# Revit family: Sanitary_Bath_Spas_Johnson-Suisse_Select_Mk_II_1600_Bath
name_source: partatom
category: Plumbing Fixtures
revit_build: Autodesk Revit 2015 (Build: 20140606_1530(x64)
units: mm (PartAtom-declared; Revit-internal decimal feet)

## types (1)
- Select Mk II 1600 Bath
    BIMobject category = Bath & Spas
    Brand url = http://www.johnsonsuisse.com.au
    Default Elevation = 1219 mm
    Design country = China
    EAN code = https://9325304005621
    Edition number = 1
    IFC Classification = Sanitary Terminal
    Manufacturer country = China
    Manufacturer name = Johnson Suisse
    Material main = Acrylic
    NBS Reference Code = 35-06-08
    NBS Reference Description = Baths
    Nominal height = 420 mm  [stored 1.37795 ft]
    Nominal width = 1660 mm  [stored 5.44619 ft]
    Product Guid = 1ae362b3-3b77-4cad-9836-f70f2127e520
    Product SKU = J5166
    Product data url = https://bimobject.com
    Product family = Select
    Product group = Baths
    Product url = https://johnsonsuisse.com.au
    QR code = http://bimobject.com
    Technical description = https://johnsonsuisse.com.au
    Type = select_mk_ii_1600_bath : Default
    UNSPSC Code = 30181501
    Uniclass 1.4 Code = L7211
    Uniclass 1.4 Description = Baths
    Uniclass 2.0 Code = PR-35-06-08
    Uniclass 2.0 Description = Baths
    Uniclass 2015 Code = Pr_40_20_06_08
    Uniclass 2015 Name = Baths
    Weight Net (Kg) = 17

note: [stored X ft] marks values corroborated as IEEE doubles in the binary element streams (Revit-internal decimal feet)

## geometry (parser evidence)
native form markers: Sweep x4
no freeform markers — native parametric forms only
